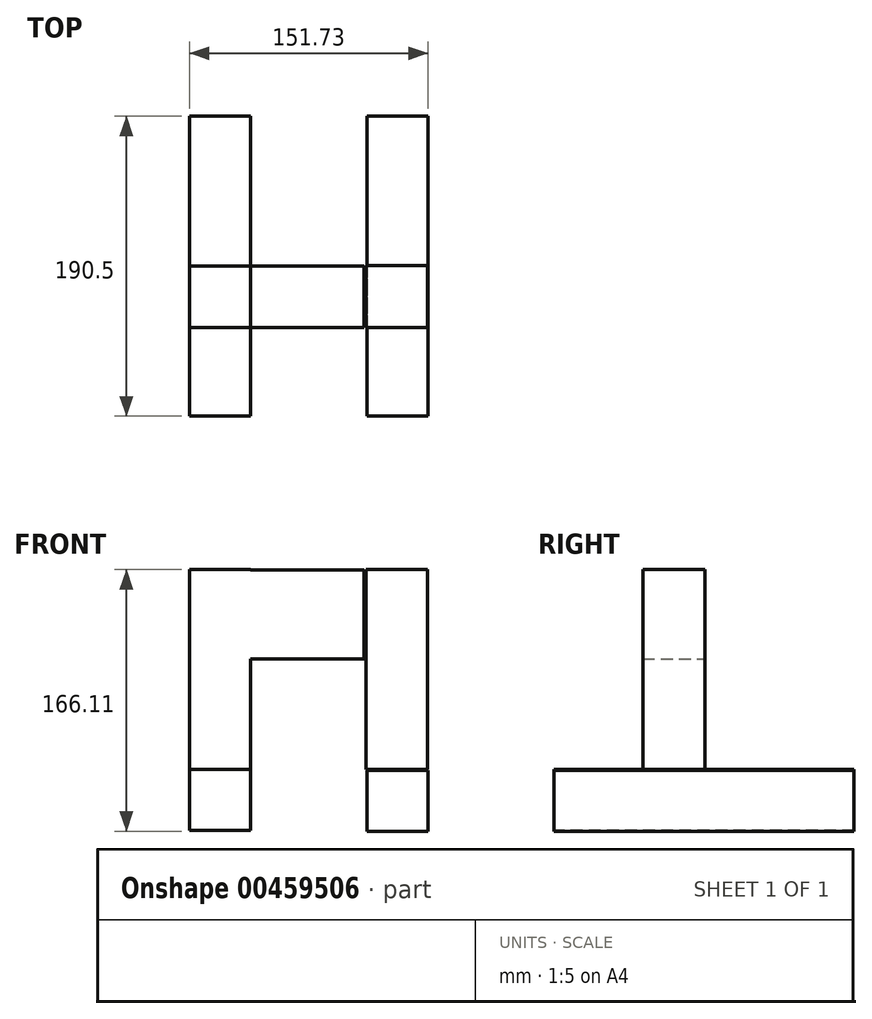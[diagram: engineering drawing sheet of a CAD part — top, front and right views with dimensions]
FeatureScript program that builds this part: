
annotation { "Feature Type Name" : "Feature", "Feature Type Description" : "" }
export const myFeature = defineFeature(function(context is Context, id is Id, definition is map)
    precondition{}
    {
        {
            var Q0;
            Q0=qCreatedBy(makeId("Front.planeOp"),FACE);
            var sketch = newSketch(context, id + "F0", { "sketchPlane" : qUnion([Q0])});
            skLineSegment(sketch, "E0.bottom", {"start": v(-75.86, -75.16) * mm, "end": v(-37.12, -75.16) * mm});
            skLineSegment(sketch, "E0.top", {"start": v(-75.86, -36.54) * mm, "end": v(-37.12, -36.54) * mm});
            skLineSegment(sketch, "E0.left", {"start": v(-75.86, -75.16) * mm, "end": v(-75.86, -36.54) * mm});
            skLineSegment(sketch, "E0.right", {"start": v(-37.12, -75.16) * mm, "end": v(-37.12, -36.54) * mm});
            skLineSegment(sketch, "E1.bottom", {"start": v(37.14, -75.65) * mm, "end": v(75.87, -75.65) * mm});
            skLineSegment(sketch, "E1.top", {"start": v(37.14, -37.03) * mm, "end": v(75.87, -37.03) * mm});
            skLineSegment(sketch, "E1.left", {"start": v(37.14, -75.65) * mm, "end": v(37.14, -37.03) * mm});
            skLineSegment(sketch, "E1.right", {"start": v(75.87, -75.65) * mm, "end": v(75.87, -37.03) * mm});
            skSolve(sketch);
        }
        {
            var Q0;
            Q0=makeQuery(id+"F0.imprint","IMPRINT",FACE,{"disambiguationData":[TD([[makeQuery(id+"F0.imprint","IMPRINT",EDGE,{"derivedFrom":sQuery(id+"F0.wireOp",EDGE,"E0.bottom")}),1.0]])]});
            var Q1;
            Q1=makeQuery(id+"F0.imprint","IMPRINT",FACE,{"disambiguationData":[TD([[makeQuery(id+"F0.imprint","IMPRINT",EDGE,{"derivedFrom":sQuery(id+"F0.wireOp",EDGE,"E1.bottom")}),1.0]])]});
            extrude(context, id + "F1", {"entities" : qUnion([Q0, Q1]), "oppositeDirection" : true, "depth" : 190.5 * mm});
        }
        {
            var Q0;
            Q0=makeQuery(id+"F1.opExtrude","SWEPT_FACE",FACE,{"disambiguationData":[OSD([sQuery(id+"F0.wireOp",EDGE,"E0.top")])]});
            var sketch = newSketch(context, id + "F2", { "sketchPlane" : qUnion([Q0])});
            skLineSegment(sketch, "E2.bottom", {"start": v(-75.86, 95.25) * mm, "end": v(-37.12, 95.25) * mm});
            skLineSegment(sketch, "E2.top", {"start": v(-75.86, 56.3) * mm, "end": v(-37.12, 56.3) * mm});
            skLineSegment(sketch, "E2.left", {"start": v(-75.86, 95.25) * mm, "end": v(-75.86, 56.3) * mm});
            skLineSegment(sketch, "E2.right", {"start": v(-37.12, 95.25) * mm, "end": v(-37.12, 56.3) * mm});
            skLineSegment(sketch, "E3.bottom", {"start": v(36.42, 56.3) * mm, "end": v(75.39, 56.3) * mm});
            skLineSegment(sketch, "E3.top", {"start": v(36.42, 95.66) * mm, "end": v(75.39, 95.66) * mm});
            skLineSegment(sketch, "E3.left", {"start": v(36.42, 56.3) * mm, "end": v(36.42, 95.66) * mm});
            skLineSegment(sketch, "E3.right", {"start": v(75.39, 56.3) * mm, "end": v(75.39, 95.66) * mm});
            skSolve(sketch);
        }
        {
            var Q0;
            Q0=makeQuery(id+"F2.imprint","IMPRINT",FACE,{"disambiguationData":[TD([[makeQuery(id+"F2.imprint","IMPRINT",EDGE,{"derivedFrom":sQuery(id+"F2.wireOp",EDGE,"E2.bottom")}),-1.0]])]});
            var Q1;
            Q1=makeQuery(id+"F2.imprint","IMPRINT",FACE,{"disambiguationData":[TD([[makeQuery(id+"F2.imprint","IMPRINT",EDGE,{"derivedFrom":sQuery(id+"F2.wireOp",EDGE,"E3.bottom")}),1.0]])]});
            extrude(context, id + "F3", {"entities" : qUnion([Q0, Q1]), "operationType" : NewBodyOperationType.ADD, "depth" : 127 * mm});
        }
        {
            var Q0;
            Q0=makeQuery(id+"F3.boolean.opBoolean","MERGE",FACE,{"derivedFrom":[makeQuery(id+"F1.opExtrude","SWEPT_FACE",FACE,{"disambiguationData":[OSD([sQuery(id+"F0.wireOp",EDGE,"E0.right")])]}),makeQuery(id+"F3.opExtrude","SWEPT_FACE",FACE,{"disambiguationData":[OSD([sQuery(id+"F2.wireOp",EDGE,"E2.right")])]})]});
            var sketch = newSketch(context, id + "F4", { "sketchPlane" : qUnion([Q0])});
            skSolve(sketch);
        }
        {
            var Q0;
            {var subQ2=sQuery(id+"F0.wireOp",EDGE,"E0.right");Q0=makeQuery(id+"F4.imprint","IMPRINT",FACE,{"disambiguationData":[TD([[makeQuery(id+"F4.imprint","IMPRINT",EDGE,{"derivedFrom":makeQuery(id+"F1.opExtrude","CAP_EDGE",EDGE,{"disambiguationData":[OSD([subQ2])],"isStart":true})}),-1.0]])]});}
            var sketch = newSketch(context, id + "F5", { "sketchPlane" : qUnion([Q0])});
            skLineSegment(sketch, "E4.bottom", {"start": v(55.7, 90.28) * mm, "end": v(97.97, 90.28) * mm});
            skLineSegment(sketch, "E4.top", {"start": v(55.7, 33.9) * mm, "end": v(97.97, 33.9) * mm});
            skLineSegment(sketch, "E4.left", {"start": v(55.7, 90.28) * mm, "end": v(55.7, 33.9) * mm});
            skLineSegment(sketch, "E4.right", {"start": v(97.97, 90.28) * mm, "end": v(97.97, 33.9) * mm});
            skPoint(sketch, "E4.middle", {"position": v(76.83, 62.09) * mm});
            skSolve(sketch);
        }
        {
            var Q0;
            {var subQ0=sQuery(id+"F5.wireOp",EDGE,"E4.bottom");var subQ1=sQuery(id+"F2.wireOp",EDGE,"E2.right");var subQ2=sQuery(id+"F0.wireOp",EDGE,"E0.right");var subQ3=sQuery(id+"F0.wireOp",EDGE,"E0.top");var subQ4=makeQuery(id+"F4.imprint","IMPRINT",EDGE,{"derivedFrom":makeQuery(id+"F3.opExtrude","SWEPT_EDGE",EDGE,{"disambiguationData":[OSD([subQ3,subQ2,sQuery(id+"F2.wireOp",EDGE,"E2.top"),subQ1])]})});var subQ5=makeQuery(id+"F5.imprint","INTERSECT",VERTEX,{"derivedFrom":[subQ4,subQ0]});Q0=makeQuery(id+"F5.imprint","IMPRINT",FACE,{"disambiguationData":[TD([[makeQuery(id+"F5.imprint","IMPRINT",EDGE,{"disambiguationData":[TD([[subQ5,-1.0]])],"derivedFrom":subQ0}),-1.0]])]});}
            extrude(context, id + "F6", {"entities" : qUnion([Q0]), "operationType" : NewBodyOperationType.ADD, "depth" : 72.14 * mm});
        }
    });
